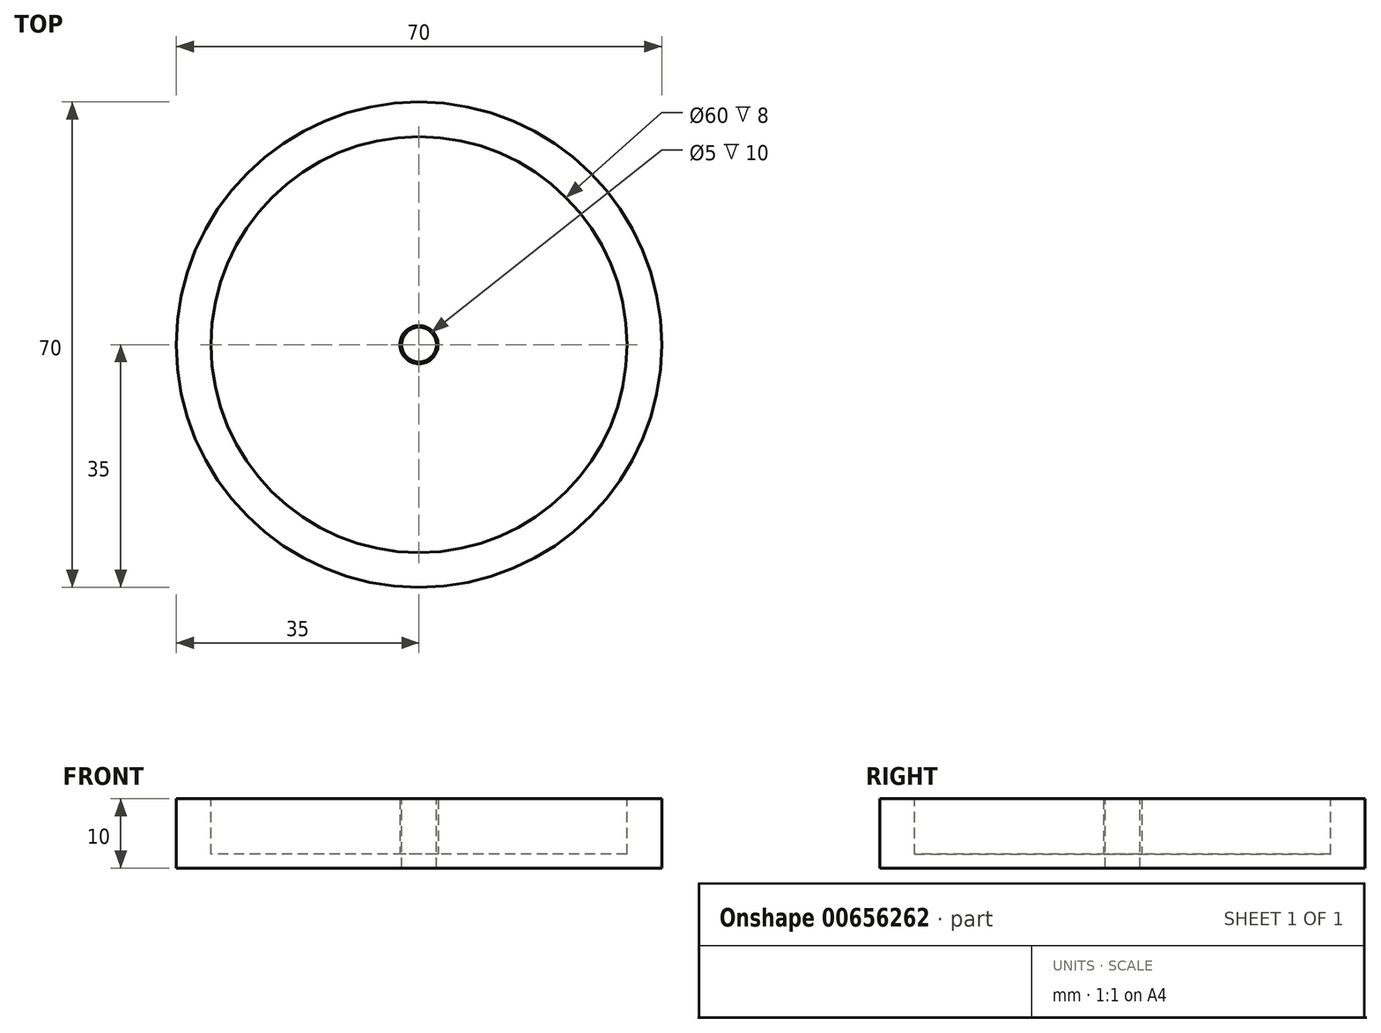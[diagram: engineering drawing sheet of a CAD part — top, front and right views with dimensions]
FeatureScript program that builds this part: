
annotation { "Feature Type Name" : "Feature", "Feature Type Description" : "" }
export const myFeature = defineFeature(function(context is Context, id is Id, definition is map)
    precondition{}
    {
        {
            var Q0;
            Q0=qCreatedBy(makeId("Top.planeOp"),FACE);
            var sketch = newSketch(context, id + "F0", { "sketchPlane" : qUnion([Q0])});
            skCircle(sketch, "E0", {"center": v(0, 0) * mm, "radius": 35 * mm});
            skSolve(sketch);
        }
        {
            var Q0;
            Q0=makeQuery(id+"F0.imprint","IMPRINT",FACE,{"disambiguationData":[TD([[makeQuery(id+"F0.imprint","IMPRINT",EDGE,{"derivedFrom":sQuery(id+"F0.wireOp",EDGE,"E0")}),1.0]])]});
            extrude(context, id + "F1", {"entities" : qUnion([Q0]), "depth" : 10 * mm, "offsetDistance" : 25 * mm});
        }
        {
            var Q0;
            Q0=makeQuery(id+"F1.opExtrude","CAP_FACE",FACE,{"disambiguationData":[OSD([sQuery(id+"F0.wireOp",EDGE,"E0")])],"isStart":false});
            var sketch = newSketch(context, id + "F2", { "sketchPlane" : qUnion([Q0])});
            skCircle(sketch, "E1", {"center": v(0, 0) * mm, "radius": 30 * mm});
            skSolve(sketch);
        }
        {
            var Q0;
            Q0=makeQuery(id+"F2.imprint","IMPRINT",FACE,{"disambiguationData":[TD([[makeQuery(id+"F2.imprint","IMPRINT",EDGE,{"derivedFrom":sQuery(id+"F2.wireOp",EDGE,"E1")}),1.0]])]});
            var Q1;
            Q1=sQuery(id+"F2.wireOp",EDGE,"E1");
            extrude(context, id + "F3", {"entities" : qUnion([Q0]), "operationType" : NewBodyOperationType.REMOVE, "surfaceEntities" : qUnion([Q1]), "oppositeDirection" : true, "depth" : 8 * mm, "offsetDistance" : 25 * mm});
        }
        {
            var Q0;
            Q0=makeQuery(id+"F3.boolean.opBoolean","COPY",FACE,{"derivedFrom":makeQuery(id+"F3.opExtrude","CAP_FACE",FACE,{"disambiguationData":[OSD([sQuery(id+"F2.wireOp",EDGE,"E1")])],"isStart":false})});
            var sketch = newSketch(context, id + "F4", { "sketchPlane" : qUnion([Q0])});
            skCircle(sketch, "E2", {"center": v(0, 0) * mm, "radius": 2.75 * mm});
            skSolve(sketch);
        }
        {
            var Q0;
            Q0 = qSketchRegion(id + "F4", true);
            extrude(context, id + "F5", {"entities" : qUnion([Q0]), "operationType" : NewBodyOperationType.ADD, "depth" : 8 * mm, "offsetDistance" : 25 * mm});
        }
        {
            var Q0;
            Q0=makeQuery(id+"F5.opExtrude","CAP_FACE",FACE,{"disambiguationData":[OSD([sQuery(id+"F4.wireOp",EDGE,"E2")])],"isStart":false});
            var sketch = newSketch(context, id + "F6", { "sketchPlane" : qUnion([Q0])});
            skCircle(sketch, "E3", {"center": v(0, 0) * mm, "radius": 2.5 * mm});
            skSolve(sketch);
        }
        {
            var Q0;
            Q0 = qSketchRegion(id + "F6", true);
            extrude(context, id + "F7", {"entities" : qUnion([Q0]), "operationType" : NewBodyOperationType.REMOVE, "oppositeDirection" : true, "depth" : 10 * mm, "offsetDistance" : 25 * mm});
        }
    });
